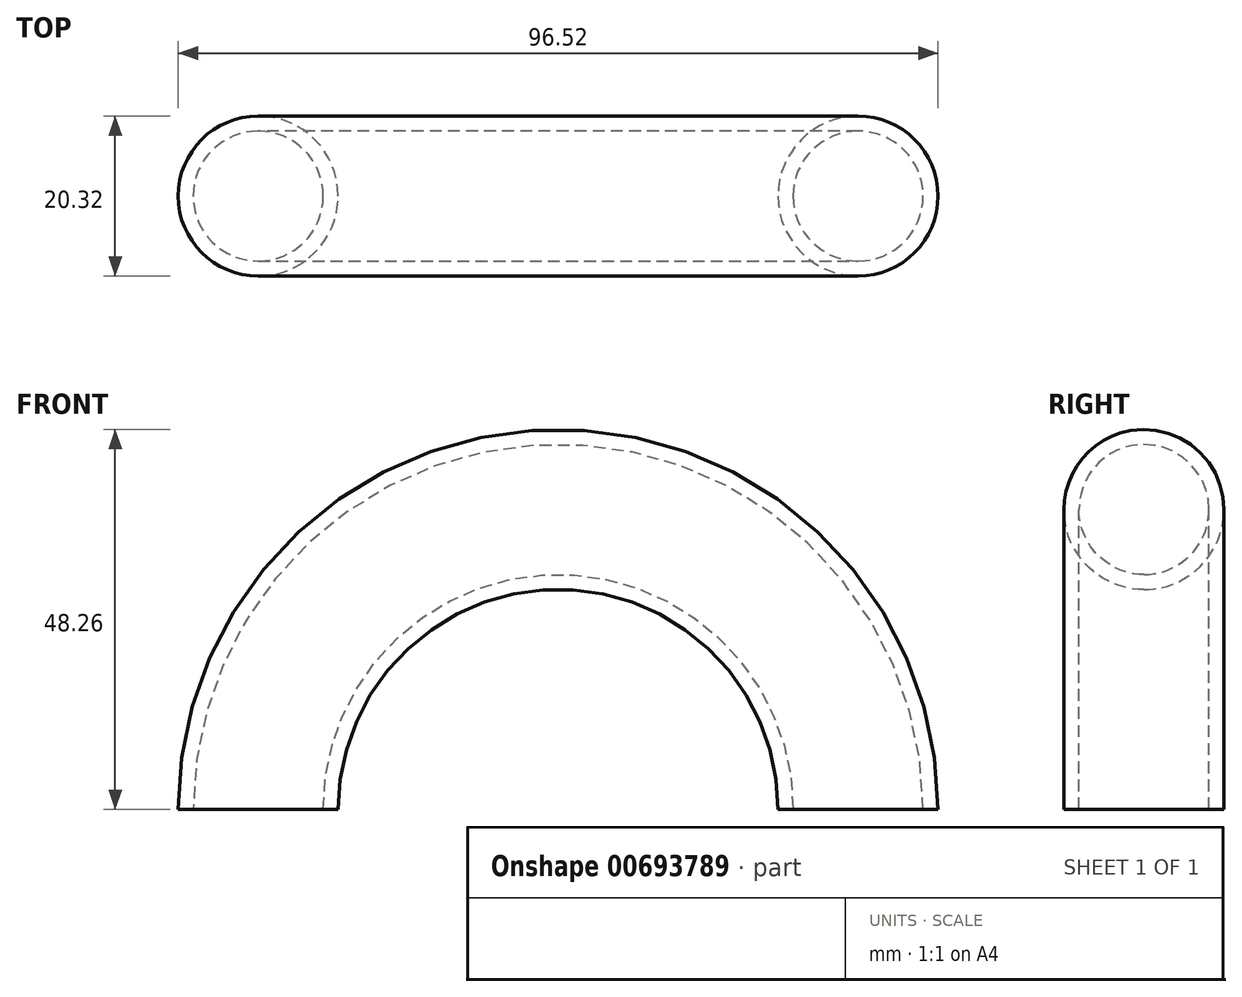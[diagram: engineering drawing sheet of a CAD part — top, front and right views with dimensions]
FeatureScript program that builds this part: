
annotation { "Feature Type Name" : "Feature", "Feature Type Description" : "" }
export const myFeature = defineFeature(function(context is Context, id is Id, definition is map)
    precondition{}
    {
        {
            var Q0;
            Q0=qCreatedBy(makeId("Top.planeOp"),FACE);
            var sketch = newSketch(context, id + "F0", { "sketchPlane" : qUnion([Q0])});
            skCircle(sketch, "E0", {"center": v(0, 0) * mm, "radius": 8.26 * mm});
            skCircle(sketch, "E1", {"center": v(0, 0) * mm, "radius": 10.16 * mm});
            skSolve(sketch);
        }
        {
            var Q0;
            Q0=qCreatedBy(makeId("Front.planeOp"),FACE);
            var sketch = newSketch(context, id + "F1", { "sketchPlane" : qUnion([Q0])});
            skArc(sketch, "E2", {"start": v(76.2, 0) * mm, "mid": v(38.1, 38.1) * mm, "end": v(0, 0) * mm});
            skSolve(sketch);
        }
        {
            var Q0;
            Q0=makeQuery(id+"F0.imprint","IMPRINT",FACE,{"disambiguationData":[TD([[makeQuery(id+"F0.imprint","IMPRINT",EDGE,{"derivedFrom":sQuery(id+"F0.wireOp",EDGE,"E0")}),-1.0]])]});
            var Q1;
            Q1=sQuery(id+"F1.wireOp",EDGE,"E2");
            sweep(context, id + "F2", {"profiles" : qUnion([Q0]), "path" : qUnion([Q1])});
        }
    });
